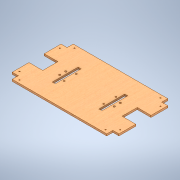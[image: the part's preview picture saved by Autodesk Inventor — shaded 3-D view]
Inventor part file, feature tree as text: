
AUTODESK INVENTOR PART (.ipt)
format: ipt  version: 2020 (Build 240168000, 168)  size: 237,056 bytes
history: native  units: mm
features: sketch x5, extrude x3, hole x2
ambient origin geometry x8: Origin, YZ Plane, XZ Plane, XY Plane, X Axis, Y Axis, Z Axis, Center Point
bodies: Body1 (feature_tree)
feature tree (10):
  extrude  "Extrusion2"  Depth=350.0mm
  extrude  "Extrusion3"  Depth=200.0mm
  hole  "Perçage2"  [1 undecoded]
  extrude  "Extrusion4"  Depth=20.0mm
  hole  "Perçage3"  [1 undecoded]
  sketch  "Esquisse1"
  sketch  "Esquisse3"
  sketch  "Esquisse4"
  sketch  "Esquisse5"
  sketch  "Esquisse6"
note: 2 required parameter values undecoded (feature->parameter linkage not recoverable at this tier; creation-order binding heuristic only, values carry confidence <= 0.55)
